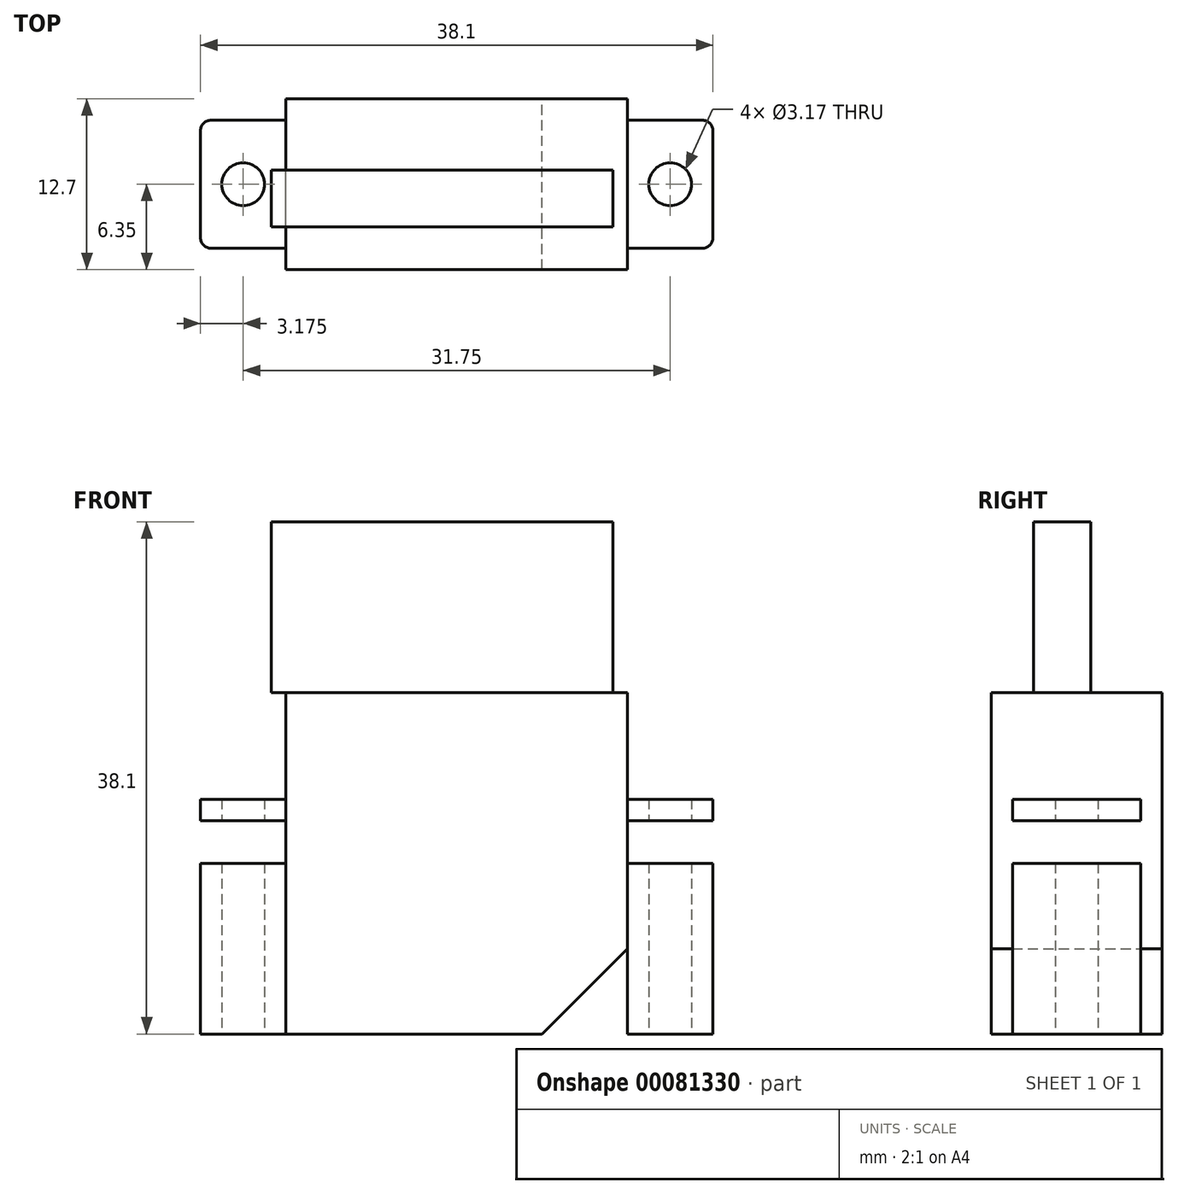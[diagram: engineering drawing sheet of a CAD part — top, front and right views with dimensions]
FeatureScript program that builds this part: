
annotation { "Feature Type Name" : "Feature", "Feature Type Description" : "" }
export const myFeature = defineFeature(function(context is Context, id is Id, definition is map)
    precondition{}
    {
        {
            var Q0;
            Q0=qCreatedBy(makeId("Front.planeOp"),FACE);
            var sketch = newSketch(context, id + "F0", { "sketchPlane" : qUnion([Q0])});
            skLineSegment(sketch, "E0", {"start": v(0, 0) * mm, "end": v(0, 25.4) * mm});
            skLineSegment(sketch, "E1", {"start": v(0, 25.4) * mm, "end": v(25.4, 25.4) * mm});
            skLineSegment(sketch, "E2", {"start": v(25.4, 25.4) * mm, "end": v(25.4, 6.35) * mm});
            skLineSegment(sketch, "E3", {"start": v(25.4, 6.35) * mm, "end": v(19.05, 0) * mm});
            skLineSegment(sketch, "E4", {"start": v(19.05, 0) * mm, "end": v(0, 0) * mm});
            skSolve(sketch);
        }
        {
            var Q0;
            Q0=qSketchRegion(id+"F0",true);
            extrude(context, id + "F1", {"entities" : qUnion([Q0]), "depth" : 12.7 * mm});
        }
        {
            var Q0;
            Q0=makeQuery(id+"F1.opExtrude","SWEPT_FACE",FACE,{"disambiguationData":[OSD([sQuery(id+"F0.wireOp",EDGE,"E1")])]});
            cPlane(context, id + "F2", {"entities" : qUnion([Q0]), "cplaneType" : CPlaneType.OFFSET, "offset" : 9.52 * mm, "oppositeDirection" : true, "width" : 152.4 * mm, "height" : 152.4 * mm});
        }
        {
            var Q0;
            Q0=qCreatedBy(id+"F2.planeOp",FACE);
            var sketch = newSketch(context, id + "F3", { "sketchPlane" : qUnion([Q0])});
            skLineSegment(sketch, "E5", {"start": v(0, -1.59) * mm, "end": v(-6.35, -1.59) * mm});
            skLineSegment(sketch, "E6", {"start": v(-6.35, -1.59) * mm, "end": v(-6.35, -11.11) * mm});
            skLineSegment(sketch, "E7", {"start": v(-6.35, -11.11) * mm, "end": v(0, -11.11) * mm});
            skLineSegment(sketch, "E8", {"start": v(0, -11.11) * mm, "end": v(0, -1.59) * mm});
            skCircle(sketch, "E9", {"center": v(-3.17, -6.35) * mm, "radius": 1.59 * mm});
            skLineSegment(sketch, "E10", {"start": v(12.7, 7.88) * mm, "end": v(12.7, -17.32) * mm, "construction": true});
            skLineSegment(sketch, "E11.0.MirrorCS", {"start": v(25.4, -11.11) * mm, "end": v(25.4, -1.59) * mm});
            skLineSegment(sketch, "E11.1.MirrorCS", {"start": v(31.75, -11.11) * mm, "end": v(25.4, -11.11) * mm});
            skLineSegment(sketch, "E11.2.MirrorCS", {"start": v(25.4, -1.59) * mm, "end": v(31.75, -1.59) * mm});
            skLineSegment(sketch, "E11.3.MirrorCS", {"start": v(31.75, -1.59) * mm, "end": v(31.75, -11.11) * mm});
            skCircle(sketch, "E11.4.MirrorC", {"center": v(28.57, -6.35) * mm, "radius": 1.59 * mm});
            skSolve(sketch);
        }
        {
            var Q0;
            Q0=makeQuery(id+"F3.imprint","IMPRINT",FACE,{"disambiguationData":[TD([[makeQuery(id+"F3.imprint","IMPRINT",EDGE,{"derivedFrom":sQuery(id+"F3.wireOp",EDGE,"E5")}),1.0]])]});
            extrude(context, id + "F4", {"entities" : qUnion([Q0]), "operationType" : NewBodyOperationType.ADD, "depth" : 1.59 * mm});
        }
        {
            var Q0;
            Q0=makeQuery(id+"F3.imprint","IMPRINT",FACE,{"disambiguationData":[TD([[makeQuery(id+"F3.imprint","IMPRINT",EDGE,{"derivedFrom":sQuery(id+"F3.wireOp",EDGE,"E11.0.MirrorCS")}),-1.0]])]});
            extrude(context, id + "F5", {"entities" : qUnion([Q0]), "operationType" : NewBodyOperationType.ADD, "depth" : 1.59 * mm});
        }
        {
            var Q0;
            Q0=makeQuery(id+"F5.opExtrude","SWEPT_EDGE",EDGE,{"disambiguationData":[OSD([sQuery(id+"F3.wireOp",EDGE,"E11.1.MirrorCS"),sQuery(id+"F3.wireOp",EDGE,"E11.3.MirrorCS")])]});
            var Q1;
            Q1=makeQuery(id+"F4.opExtrude","SWEPT_EDGE",EDGE,{"disambiguationData":[OSD([sQuery(id+"F3.wireOp",EDGE,"E6"),sQuery(id+"F3.wireOp",EDGE,"E7")])]});
            var Q2;
            Q2=makeQuery(id+"F5.opExtrude","SWEPT_EDGE",EDGE,{"disambiguationData":[OSD([sQuery(id+"F3.wireOp",EDGE,"E11.2.MirrorCS"),sQuery(id+"F3.wireOp",EDGE,"E11.3.MirrorCS")])]});
            var Q3;
            Q3=makeQuery(id+"F4.opExtrude","SWEPT_EDGE",EDGE,{"disambiguationData":[OSD([sQuery(id+"F3.wireOp",EDGE,"E5"),sQuery(id+"F3.wireOp",EDGE,"E6")])]});
            fillet(context, id + "F6", {"entities" : qUnion([Q0, Q1, Q2, Q3]), "radius" : 0.8 * mm, "tangentPropagation" : true, "allowEdgeOverflow" : false});
        }
        {
            var Q0;
            Q0=qCreatedBy(makeId("Top.planeOp"),FACE);
            var sketch = newSketch(context, id + "F7", { "sketchPlane" : qUnion([Q0])});
            skLineSegment(sketch, "E12.0.0", {"start": v(25.4, -11.11) * mm, "end": v(30.96, -11.11) * mm});
            skArc(sketch, "E12.0.1", {"start": v(30.96, -11.11) * mm, "mid": v(31.52, -10.88) * mm, "end": v(31.75, -10.32) * mm});
            skLineSegment(sketch, "E12.0.2", {"start": v(31.75, -10.32) * mm, "end": v(31.75, -2.38) * mm});
            skArc(sketch, "E12.0.3", {"start": v(31.75, -2.38) * mm, "mid": v(31.52, -1.82) * mm, "end": v(30.96, -1.59) * mm});
            skLineSegment(sketch, "E12.0.4", {"start": v(30.96, -1.59) * mm, "end": v(25.4, -1.59) * mm});
            skLineSegment(sketch, "E12.0.5", {"start": v(25.4, -1.59) * mm, "end": v(25.4, -11.11) * mm});
            skLineSegment(sketch, "E13.0.0", {"start": v(0, -1.59) * mm, "end": v(-5.56, -1.59) * mm});
            skArc(sketch, "E13.0.1", {"start": v(-5.56, -1.59) * mm, "mid": v(-6.12, -1.82) * mm, "end": v(-6.35, -2.38) * mm});
            skLineSegment(sketch, "E13.0.2", {"start": v(-6.35, -2.38) * mm, "end": v(-6.35, -10.32) * mm});
            skArc(sketch, "E13.0.3", {"start": v(-6.35, -10.32) * mm, "mid": v(-6.12, -10.88) * mm, "end": v(-5.56, -11.11) * mm});
            skLineSegment(sketch, "E13.0.4", {"start": v(-5.56, -11.11) * mm, "end": v(0, -11.11) * mm});
            skLineSegment(sketch, "E13.0.5", {"start": v(0, -11.11) * mm, "end": v(0, -1.59) * mm});
            skCircle(sketch, "E14.1", {"center": v(28.57, -6.35) * mm, "radius": 1.59 * mm});
            skCircle(sketch, "E15.2", {"center": v(-3.17, -6.35) * mm, "radius": 1.59 * mm});
            skSolve(sketch);
        }
        {
            var Q0;
            Q0=makeQuery(id+"F7.imprint","IMPRINT",FACE,{"disambiguationData":[TD([[makeQuery(id+"F7.imprint","IMPRINT",EDGE,{"derivedFrom":sQuery(id+"F7.wireOp",EDGE,"E12.0.0")}),1.0]])]});
            var Q1;
            Q1=makeQuery(id+"F7.imprint","IMPRINT",FACE,{"disambiguationData":[TD([[makeQuery(id+"F7.imprint","IMPRINT",EDGE,{"derivedFrom":sQuery(id+"F7.wireOp",EDGE,"E13.0.0")}),1.0]])]});
            extrude(context, id + "F8", {"entities" : qUnion([Q0, Q1]), "depth" : 12.7 * mm});
        }
        {
            var Q0;
            Q0=makeQuery(id+"F1.opExtrude","SWEPT_FACE",FACE,{"disambiguationData":[OSD([sQuery(id+"F0.wireOp",EDGE,"E1")])]});
            var sketch = newSketch(context, id + "F9", { "sketchPlane" : qUnion([Q0])});
            skLineSegment(sketch, "E16.bottom", {"start": v(-1.1, -9.53) * mm, "end": v(24.3, -9.53) * mm});
            skLineSegment(sketch, "E16.top", {"start": v(-1.1, -5.3) * mm, "end": v(24.3, -5.3) * mm});
            skLineSegment(sketch, "E16.left", {"start": v(-1.1, -9.53) * mm, "end": v(-1.1, -5.3) * mm});
            skLineSegment(sketch, "E16.right", {"start": v(24.3, -9.53) * mm, "end": v(24.3, -5.3) * mm});
            skSolve(sketch);
        }
        {
            var Q0;
            {var subQ0=sQuery(id+"F9.wireOp",EDGE,"E16.right");Q0=makeQuery(id+"F9.imprint","IMPRINT",FACE,{"disambiguationData":[TD([[makeQuery(id+"F9.imprint","IMPRINT",EDGE,{"derivedFrom":subQ0}),1.0]])]});}
            var Q1;
            {var subQ0=sQuery(id+"F9.wireOp",EDGE,"E16.left");Q1=makeQuery(id+"F9.imprint","IMPRINT",FACE,{"disambiguationData":[TD([[makeQuery(id+"F9.imprint","IMPRINT",EDGE,{"derivedFrom":subQ0}),-1.0]])]});}
            extrude(context, id + "F10", {"entities" : qUnion([Q0, Q1]), "depth" : 12.7 * mm});
        }
    });
